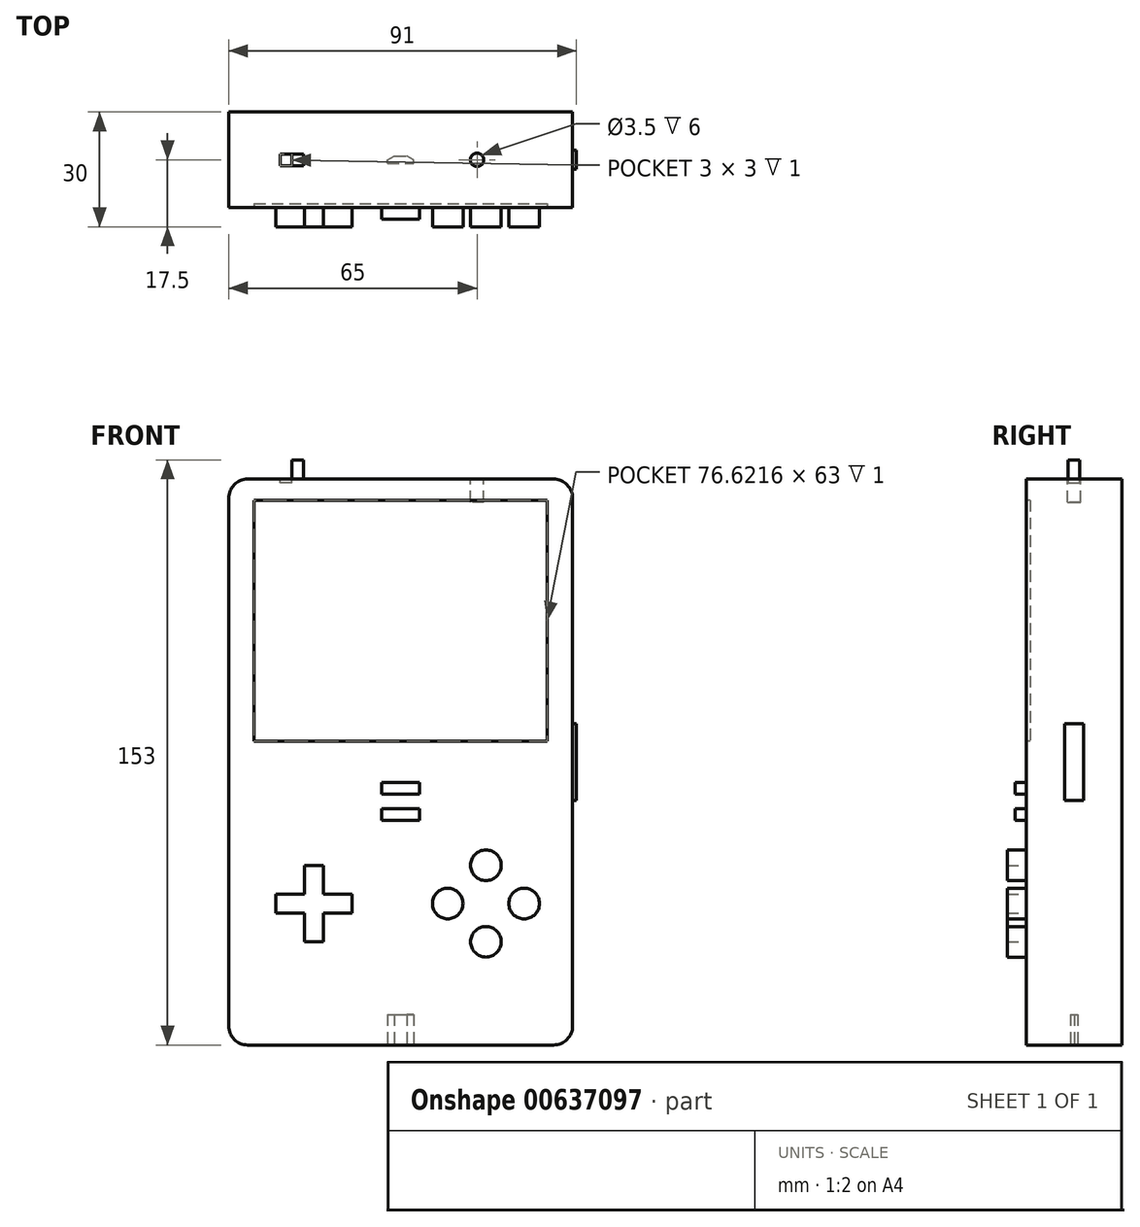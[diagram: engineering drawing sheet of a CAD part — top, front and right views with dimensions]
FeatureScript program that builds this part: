
annotation { "Feature Type Name" : "Feature", "Feature Type Description" : "" }
export const myFeature = defineFeature(function(context is Context, id is Id, definition is map)
    precondition{}
    {
        {
            var Q0;
            Q0=qCreatedBy(makeId("Front.planeOp"),FACE);
            var sketch = newSketch(context, id + "F0", { "sketchPlane" : qUnion([Q0])});
            skLineSegment(sketch, "E0.bottom", {"start": v(40, -74) * mm, "end": v(-40, -74) * mm});
            skLineSegment(sketch, "E0.top", {"start": v(40, 74) * mm, "end": v(-40, 74) * mm});
            skLineSegment(sketch, "E0.left", {"start": v(45, -69) * mm, "end": v(45, 69) * mm});
            skLineSegment(sketch, "E0.right", {"start": v(-45, -69) * mm, "end": v(-45, 69) * mm});
            skPoint(sketch, "E0.middle", {"position": v(0, 0) * mm});
            skPoint(sketch, "E1.visualSharp", {"position": v(-45, 74) * mm});
            skArc(sketch, "E1.filletArc", {"start": v(-40, 74) * mm, "mid": v(-43.54, 72.54) * mm, "end": v(-45, 69) * mm});
            skPoint(sketch, "E2.visualSharp", {"position": v(45, 74) * mm});
            skArc(sketch, "E2.filletArc", {"start": v(45, 69) * mm, "mid": v(43.54, 72.54) * mm, "end": v(40, 74) * mm});
            skPoint(sketch, "E3.visualSharp", {"position": v(45, -74) * mm});
            skArc(sketch, "E3.filletArc", {"start": v(40, -74) * mm, "mid": v(43.54, -72.54) * mm, "end": v(45, -69) * mm});
            skPoint(sketch, "E4.visualSharp", {"position": v(-45, -74) * mm});
            skArc(sketch, "E4.filletArc", {"start": v(-45, -69) * mm, "mid": v(-43.54, -72.54) * mm, "end": v(-40, -74) * mm});
            skSolve(sketch);
        }
        {
            var Q0;
            Q0=makeQuery(id+"F0.imprint","IMPRINT",FACE,{"disambiguationData":[TD([[makeQuery(id+"F0.imprint","IMPRINT",EDGE,{"derivedFrom":sQuery(id+"F0.wireOp",EDGE,"E0.bottom")}),-1.0]])]});
            extrude(context, id + "F1", {"entities" : qUnion([Q0]), "oppositeDirection" : true, "depth" : 25 * mm, "offsetDistance" : 25 * mm});
        }
        {
            var Q0;
            Q0=makeQuery(id+"F1.opExtrude","SWEPT_FACE",FACE,{"disambiguationData":[OSD([sQuery(id+"F0.wireOp",EDGE,"E0.left")])]});
            var sketch = newSketch(context, id + "F2", { "sketchPlane" : qUnion([Q0])});
            skLineSegment(sketch, "E5.bottom", {"start": v(15, -10) * mm, "end": v(10, -10) * mm});
            skLineSegment(sketch, "E5.top", {"start": v(15, 10) * mm, "end": v(10, 10) * mm});
            skLineSegment(sketch, "E5.left", {"start": v(15, -10) * mm, "end": v(15, 10) * mm});
            skLineSegment(sketch, "E5.right", {"start": v(10, -10) * mm, "end": v(10, 10) * mm});
            skPoint(sketch, "E5.middle", {"position": v(12.5, 0) * mm});
            skPoint(sketch, "E5.middle.positionSnap0", {"position": v(12.5, 74) * mm});
            skPoint(sketch, "E5.centerSnap0", {"position": v(12.5, 74) * mm});
            skSolve(sketch);
        }
        {
            var Q0;
            Q0 = qSketchRegion(id + "F2", true);
            extrude(context, id + "F3", {"entities" : qUnion([Q0]), "operationType" : NewBodyOperationType.ADD, "depth" : 1 * mm, "offsetDistance" : 25 * mm});
        }
        {
            var Q0;
            Q0=makeQuery(id+"F1.opExtrude","CAP_FACE",FACE,{"disambiguationData":[OSD([sQuery(id+"F0.wireOp",EDGE,"E0.bottom"),sQuery(id+"F0.wireOp",EDGE,"E0.top"),sQuery(id+"F0.wireOp",EDGE,"E0.left"),sQuery(id+"F0.wireOp",EDGE,"E0.right")])],"isStart":true});
            var sketch = newSketch(context, id + "F4", { "sketchPlane" : qUnion([Q0])});
            skLineSegment(sketch, "E6", {"start": v(-38.31, 68.5) * mm, "end": v(-38.31, 5.5) * mm});
            skLineSegment(sketch, "E7", {"start": v(-38.31, 5.5) * mm, "end": v(38.31, 5.5) * mm});
            skLineSegment(sketch, "E8", {"start": v(-38.31, 68.5) * mm, "end": v(38.31, 68.5) * mm});
            skLineSegment(sketch, "E9", {"start": v(38.31, 68.5) * mm, "end": v(38.31, 5.5) * mm});
            skPoint(sketch, "E10.trimOffspring.end.orphan", {"position": v(-45, 0) * mm});
            skPoint(sketch, "E11.trimOffspring.end.orphan", {"position": v(45, 0) * mm});
            skSolve(sketch);
        }
        {
            var Q0;
            Q0=makeQuery(id+"F4.imprint","IMPRINT",FACE,{"disambiguationData":[TD([[makeQuery(id+"F4.imprint","IMPRINT",EDGE,{"derivedFrom":sQuery(id+"F4.wireOp",EDGE,"E6")}),1.0]])]});
            extrude(context, id + "F5", {"entities" : qUnion([Q0]), "operationType" : NewBodyOperationType.REMOVE, "oppositeDirection" : true, "depth" : 1 * mm, "offsetDistance" : 25 * mm});
        }
        {
            var Q0;
            Q0=makeQuery(id+"F1.opExtrude","SWEPT_FACE",FACE,{"disambiguationData":[OSD([sQuery(id+"F0.wireOp",EDGE,"E0.bottom")])]});
            var sketch = newSketch(context, id + "F6", { "sketchPlane" : qUnion([Q0])});
            skLineSegment(sketch, "E12", {"start": v(0, -11.57) * mm, "end": v(3.45, -11.57) * mm});
            skLineSegment(sketch, "E13", {"start": v(0, -11.57) * mm, "end": v(-3.45, -11.57) * mm});
            skLineSegment(sketch, "E14", {"start": v(3.45, -11.57) * mm, "end": v(3.45, -12.5) * mm});
            skLineSegment(sketch, "E15", {"start": v(-3.45, -11.57) * mm, "end": v(-3.45, -12.5) * mm});
            skLineSegment(sketch, "E16", {"start": v(-1.68, -13.42) * mm, "end": v(1.68, -13.42) * mm});
            skLineSegment(sketch, "E17", {"start": v(-3.45, -12.5) * mm, "end": v(-1.68, -13.42) * mm});
            skLineSegment(sketch, "E18", {"start": v(3.45, -12.5) * mm, "end": v(1.68, -13.42) * mm});
            skPoint(sketch, "E19.end.orphan", {"position": v(-3.45, -13.42) * mm});
            skPoint(sketch, "E20.end.orphan", {"position": v(0, -13.42) * mm});
            skPoint(sketch, "E21.start.orphan", {"position": v(0, -12.5) * mm});
            skPoint(sketch, "E22.trimOffspring.end.orphan", {"position": v(40, -12.5) * mm});
            skPoint(sketch, "E23.end.orphan", {"position": v(3.45, -13.42) * mm});
            skPoint(sketch, "E24.start.orphan", {"position": v(-40, -12.5) * mm});
            skPoint(sketch, "E25.start.orphan", {"position": v(0, 0) * mm});
            skPoint(sketch, "E26.orphan", {"position": v(0, -25) * mm});
            skSolve(sketch);
        }
        {
            var Q0;
            Q0 = qSketchRegion(id + "F6", true);
            extrude(context, id + "F7", {"entities" : qUnion([Q0]), "operationType" : NewBodyOperationType.REMOVE, "oppositeDirection" : true, "depth" : 8 * mm, "offsetDistance" : 25 * mm});
        }
        {
            var Q0;
            Q0=makeQuery(id+"F1.opExtrude","SWEPT_FACE",FACE,{"disambiguationData":[OSD([sQuery(id+"F0.wireOp",EDGE,"E0.top")])]});
            var sketch = newSketch(context, id + "F8", { "sketchPlane" : qUnion([Q0])});
            skCircle(sketch, "E27", {"center": v(20, 12.5) * mm, "radius": 3 * mm});
            skPoint(sketch, "E28.orphan", {"position": v(0, 25) * mm});
            skPoint(sketch, "E29.start.orphan", {"position": v(-40, 12.5) * mm});
            skPoint(sketch, "E30.orphan", {"position": v(40, 12.5) * mm});
            skSolve(sketch);
        }
        {
            var Q0;
            Q0=makeQuery(id+"F8.imprint","IMPRINT",FACE,{"disambiguationData":[TD([[makeQuery(id+"F8.imprint","IMPRINT",EDGE,{"derivedFrom":sQuery(id+"F8.wireOp",EDGE,"E27")}),-1.0]])]});
            var sketch = newSketch(context, id + "F9", { "sketchPlane" : qUnion([Q0])});
            skLineSegment(sketch, "E31", {"start": v(18.25, 12.5) * mm, "end": v(21.75, 12.5) * mm});
            skPoint(sketch, "E31.startSnap0", {"position": v(0, 12.5) * mm});
            skCircle(sketch, "E32", {"center": v(20, 12.5) * mm, "radius": 1.75 * mm});
            skPoint(sketch, "E33.orphan", {"position": v(-39.88, 12.5) * mm});
            skPoint(sketch, "E34.orphan", {"position": v(0, 0) * mm});
            skPoint(sketch, "E35.orphan", {"position": v(20, 0) * mm});
            skLineSegment(sketch, "E36.trimOffspring", {"start": v(40, 12.5) * mm, "end": v(40.12, 12.5) * mm});
            skPoint(sketch, "E37.orphan", {"position": v(20, 25) * mm});
            skPoint(sketch, "E38.orphan", {"position": v(0, 25) * mm});
            skPoint(sketch, "E39.orphan", {"position": v(40, 0) * mm});
            skPoint(sketch, "E40.start.orphan", {"position": v(40, 25) * mm});
            skSolve(sketch);
        }
        {
            var Q0;
            Q0 = qSketchRegion(id + "F9", true);
            extrude(context, id + "F10", {"entities" : qUnion([Q0]), "operationType" : NewBodyOperationType.REMOVE, "oppositeDirection" : true, "depth" : 6 * mm, "offsetDistance" : 25 * mm});
        }
        {
            var Q0;
            Q0=qCreatedBy(makeId("Front.planeOp"),FACE);
            var sketch = newSketch(context, id + "F11", { "sketchPlane" : qUnion([Q0])});
            skPoint(sketch, "E41.orphan", {"position": v(-45.19, 0) * mm});
            skPoint(sketch, "E42.start.orphan", {"position": v(-45.19, -37) * mm});
            skPoint(sketch, "E43.orphan", {"position": v(-45.19, -74) * mm});
            skLineSegment(sketch, "E44", {"start": v(-22.69, -27) * mm, "end": v(-25.19, -27) * mm});
            skLineSegment(sketch, "E45", {"start": v(-22.69, -27) * mm, "end": v(-20.19, -27) * mm});
            skLineSegment(sketch, "E46", {"start": v(-12.69, -37) * mm, "end": v(-12.69, -39.5) * mm});
            skLineSegment(sketch, "E47", {"start": v(-12.69, -37) * mm, "end": v(-12.69, -34.5) * mm});
            skLineSegment(sketch, "E48", {"start": v(-22.69, -47) * mm, "end": v(-20.19, -47) * mm});
            skLineSegment(sketch, "E49", {"start": v(-22.69, -47) * mm, "end": v(-25.19, -47) * mm});
            skLineSegment(sketch, "E50", {"start": v(-32.69, -37) * mm, "end": v(-32.69, -39.5) * mm});
            skLineSegment(sketch, "E51", {"start": v(-32.69, -37) * mm, "end": v(-32.69, -34.5) * mm});
            skLineSegment(sketch, "E52", {"start": v(-32.69, -34.5) * mm, "end": v(-25.19, -34.5) * mm});
            skLineSegment(sketch, "E53", {"start": v(-25.19, -27) * mm, "end": v(-25.19, -34.5) * mm});
            skLineSegment(sketch, "E54", {"start": v(-32.69, -39.5) * mm, "end": v(-25.19, -39.5) * mm});
            skLineSegment(sketch, "E55", {"start": v(-25.19, -39.5) * mm, "end": v(-25.19, -47) * mm});
            skLineSegment(sketch, "E56", {"start": v(-20.19, -47) * mm, "end": v(-20.19, -39.5) * mm});
            skLineSegment(sketch, "E57", {"start": v(-20.19, -39.5) * mm, "end": v(-12.69, -39.5) * mm});
            skLineSegment(sketch, "E58", {"start": v(-12.69, -34.5) * mm, "end": v(-20.19, -34.5) * mm});
            skLineSegment(sketch, "E59", {"start": v(-20.19, -27) * mm, "end": v(-20.19, -34.5) * mm});
            skCircle(sketch, "E60", {"center": v(32.31, -37) * mm, "radius": 4 * mm});
            skCircle(sketch, "E61", {"center": v(22.31, -47) * mm, "radius": 4 * mm});
            skCircle(sketch, "E62", {"center": v(12.31, -37) * mm, "radius": 4 * mm});
            skCircle(sketch, "E63", {"center": v(22.31, -27) * mm, "radius": 4 * mm});
            skPoint(sketch, "E64.trimOffspring.end.orphan", {"position": v(44.81, -37) * mm});
            skPoint(sketch, "E65.end.orphan", {"position": v(44.81, -74) * mm});
            skPoint(sketch, "E66.start.orphan", {"position": v(44.81, 0) * mm});
            skSolve(sketch);
        }
        {
            var Q0;
            Q0 = qSketchRegion(id + "F11", true);
            extrude(context, id + "F12", {"entities" : qUnion([Q0]), "operationType" : NewBodyOperationType.ADD, "depth" : 5 * mm, "offsetDistance" : 25 * mm});
        }
        {
            var Q0;
            Q0=makeQuery(id+"F1.opExtrude","CAP_FACE",FACE,{"disambiguationData":[OSD([sQuery(id+"F0.wireOp",EDGE,"E0.bottom"),sQuery(id+"F0.wireOp",EDGE,"E0.top"),sQuery(id+"F0.wireOp",EDGE,"E0.left"),sQuery(id+"F0.wireOp",EDGE,"E0.right"),sQuery(id+"F0.wireOp",EDGE,"E1.filletArc"),sQuery(id+"F0.wireOp",EDGE,"E2.filletArc"),sQuery(id+"F0.wireOp",EDGE,"E3.filletArc"),sQuery(id+"F0.wireOp",EDGE,"E4.filletArc")])],"isStart":true});
            var sketch = newSketch(context, id + "F13", { "sketchPlane" : qUnion([Q0])});
            skLineSegment(sketch, "E67.bottom", {"start": v(5, -8.37) * mm, "end": v(-5, -8.37) * mm});
            skLineSegment(sketch, "E67.top", {"start": v(5, -5.37) * mm, "end": v(-5, -5.37) * mm});
            skLineSegment(sketch, "E67.left", {"start": v(5, -8.37) * mm, "end": v(5, -5.37) * mm});
            skLineSegment(sketch, "E67.right", {"start": v(-5, -8.37) * mm, "end": v(-5, -5.37) * mm});
            skPoint(sketch, "E67.middle", {"position": v(0, -6.88) * mm});
            skPoint(sketch, "E68.middle", {"position": v(0, -20.62) * mm});
            skPoint(sketch, "E69.orphan", {"position": v(45, -20.62) * mm});
            skPoint(sketch, "E70.end.orphan", {"position": v(45, -27.5) * mm});
            skPoint(sketch, "E71.orphan", {"position": v(-45, -20.62) * mm});
            skPoint(sketch, "E72.start.orphan", {"position": v(-45, -27.5) * mm});
            skPoint(sketch, "E73.start.orphan", {"position": v(0, -13.75) * mm});
            skPoint(sketch, "E74.trimOffspring.end.orphan", {"position": v(45, -6.88) * mm});
            skPoint(sketch, "E75.orphan", {"position": v(45, 0) * mm});
            skPoint(sketch, "E76.start.orphan", {"position": v(45, -13.75) * mm});
            skLineSegment(sketch, "E77.bottom", {"start": v(5, -15.25) * mm, "end": v(-5, -15.25) * mm});
            skLineSegment(sketch, "E77.top", {"start": v(5, -12.25) * mm, "end": v(-5, -12.25) * mm});
            skLineSegment(sketch, "E77.left", {"start": v(5, -15.25) * mm, "end": v(5, -12.25) * mm});
            skLineSegment(sketch, "E77.right", {"start": v(-5, -15.25) * mm, "end": v(-5, -12.25) * mm});
            skPoint(sketch, "E68.right.end.orphan", {"position": v(-5, -19.13) * mm});
            skPoint(sketch, "E68.right.start.orphan", {"position": v(-5, -22.12) * mm});
            skPoint(sketch, "E68.left.end.orphan", {"position": v(5, -19.12) * mm});
            skPoint(sketch, "E68.left.start.orphan", {"position": v(5, -22.12) * mm});
            skPoint(sketch, "E78.trimOffspring.end.orphan", {"position": v(0, -27.5) * mm});
            skPoint(sketch, "E79.trimOffspring.start.orphan", {"position": v(-45, -13.75) * mm});
            skPoint(sketch, "E80.end.orphan", {"position": v(-45, -6.88) * mm});
            skPoint(sketch, "E80.start.orphan", {"position": v(-45, 0) * mm});
            skPoint(sketch, "E81.orphan", {"position": v(0, 0) * mm});
            skSolve(sketch);
        }
        {
            var Q0;
            Q0 = qSketchRegion(id + "F13", true);
            extrude(context, id + "F14", {"entities" : qUnion([Q0]), "operationType" : NewBodyOperationType.ADD, "depth" : 3 * mm, "offsetDistance" : 25 * mm});
        }
        {
            var Q0;
            Q0=makeQuery(id+"F8.imprint","IMPRINT",FACE,{"disambiguationData":[TD([[makeQuery(id+"F8.imprint","IMPRINT",EDGE,{"derivedFrom":sQuery(id+"F8.wireOp",EDGE,"E27")}),-1.0]])]});
            var sketch = newSketch(context, id + "F15", { "sketchPlane" : qUnion([Q0])});
            skLineSegment(sketch, "E82.bottom", {"start": v(-28.5, 11) * mm, "end": v(-31.5, 11) * mm});
            skLineSegment(sketch, "E82.top", {"start": v(-28.5, 14) * mm, "end": v(-31.5, 14) * mm});
            skLineSegment(sketch, "E82.left", {"start": v(-28.5, 11) * mm, "end": v(-28.5, 14) * mm});
            skLineSegment(sketch, "E82.right", {"start": v(-31.5, 11) * mm, "end": v(-31.5, 14) * mm});
            skPoint(sketch, "E82.middle", {"position": v(-30, 12.5) * mm});
            skLineSegment(sketch, "E83", {"start": v(-28.5, 14) * mm, "end": v(-25.5, 14) * mm});
            skLineSegment(sketch, "E84", {"start": v(-25.5, 14) * mm, "end": v(-25.5, 11) * mm});
            skLineSegment(sketch, "E85", {"start": v(-25.5, 11) * mm, "end": v(-28.5, 11) * mm});
            skPoint(sketch, "E86.orphan", {"position": v(-30, 25) * mm});
            skPoint(sketch, "E87.orphan", {"position": v(-40, 25) * mm});
            skPoint(sketch, "E88.orphan", {"position": v(-20, 25) * mm});
            skPoint(sketch, "E89.orphan", {"position": v(-40, 0) * mm});
            skPoint(sketch, "E90.end.orphan", {"position": v(-10, 0) * mm});
            skPoint(sketch, "E91.orphan", {"position": v(0, 12.5) * mm});
            skPoint(sketch, "E92.end.orphan", {"position": v(10, 0) * mm});
            skPoint(sketch, "E92.start.orphan", {"position": v(10, 25) * mm});
            skPoint(sketch, "E93.orphan", {"position": v(20, 0) * mm});
            skPoint(sketch, "E94.end.orphan", {"position": v(30, 0) * mm});
            skPoint(sketch, "E94.start.orphan", {"position": v(30, 25) * mm});
            skPoint(sketch, "E95.start.orphan", {"position": v(0, 0) * mm});
            skPoint(sketch, "E96.end.orphan", {"position": v(-20, 0) * mm});
            skPoint(sketch, "E97.start.orphan", {"position": v(-30, 0) * mm});
            skPoint(sketch, "E98.start.orphan", {"position": v(-10, 25) * mm});
            skPoint(sketch, "E99.orphan", {"position": v(0, 25) * mm});
            skPoint(sketch, "E100.orphan", {"position": v(20, 25) * mm});
            skPoint(sketch, "E101.trimOffspring.end.orphan", {"position": v(40, 0) * mm});
            skPoint(sketch, "E102.end.orphan", {"position": v(40, 25) * mm});
            skSolve(sketch);
        }
        {
            var Q0;
            Q0=makeQuery(id+"F15.imprint","IMPRINT",FACE,{"disambiguationData":[TD([[makeQuery(id+"F15.imprint","IMPRINT",EDGE,{"derivedFrom":sQuery(id+"F15.wireOp",EDGE,"E82.bottom")}),-1.0]])]});
            var Q1;
            Q1=sQuery(id+"F15.wireOp",EDGE,"E82.top");
            var Q2;
            Q2=sQuery(id+"F15.wireOp",EDGE,"E82.right");
            var Q3;
            Q3=sQuery(id+"F15.wireOp",EDGE,"E82.bottom");
            var Q4;
            Q4=sQuery(id+"F15.wireOp",EDGE,"E82.left");
            extrude(context, id + "F16", {"entities" : qUnion([Q0]), "operationType" : NewBodyOperationType.REMOVE, "surfaceEntities" : qUnion([Q1, Q2, Q3, Q4]), "oppositeDirection" : true, "depth" : 1 * mm, "offsetDistance" : 25 * mm});
        }
        {
            var Q0;
            Q0=makeQuery(id+"F8.imprint","IMPRINT",FACE,{"disambiguationData":[TD([[makeQuery(id+"F8.imprint","IMPRINT",EDGE,{"derivedFrom":sQuery(id+"F8.wireOp",EDGE,"E27")}),-1.0]])]});
            var sketch = newSketch(context, id + "F17", { "sketchPlane" : qUnion([Q0])});
            skLineSegment(sketch, "E103.left", {"start": v(-28.47, 10.96) * mm, "end": v(-28.47, 13.96) * mm});
            skPoint(sketch, "E103.middle", {"position": v(-29.97, 12.46) * mm});
            skLineSegment(sketch, "E104", {"start": v(-28.47, 13.96) * mm, "end": v(-25.47, 13.96) * mm});
            skLineSegment(sketch, "E105", {"start": v(-25.47, 13.96) * mm, "end": v(-25.47, 10.96) * mm});
            skLineSegment(sketch, "E106", {"start": v(-25.47, 10.96) * mm, "end": v(-28.47, 10.96) * mm});
            skPoint(sketch, "E103.right.end.orphan", {"position": v(-31.47, 13.96) * mm});
            skPoint(sketch, "E103.bottom.end.orphan", {"position": v(-31.47, 10.96) * mm});
            skSolve(sketch);
        }
        {
            var Q0;
            Q0=makeQuery(id+"F17.imprint","IMPRINT",FACE,{"disambiguationData":[TD([[makeQuery(id+"F17.imprint","IMPRINT",EDGE,{"derivedFrom":sQuery(id+"F17.wireOp",EDGE,"E103.left")}),-1.0]])]});
            extrude(context, id + "F18", {"entities" : qUnion([Q0]), "operationType" : NewBodyOperationType.ADD, "depth" : 5 * mm, "offsetDistance" : 25 * mm});
        }
    });
